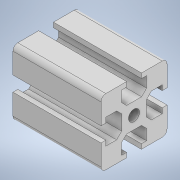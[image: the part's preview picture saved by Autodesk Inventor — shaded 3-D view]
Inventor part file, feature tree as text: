
AUTODESK INVENTOR PART (.ipt)
format: ipt  version: 2020.2 (Build 242310000, 310)  size: 175,104 bytes
history: native  units: in
note: dims shown in document units (in); Inventor stores cm internally (conversion verified against a paired STEP export)
features: extrude x1, sketch x1
ambient origin geometry x8: Origin, YZ Plane, XZ Plane, XY Plane, X Axis, Y Axis, Z Axis, Center Point
bodies: Solid1 (feature_tree)
feature tree (2):
  extrude  "Extrusion1"  Depth=0.29in
  sketch  "Sketch2"  dims[d9=0.2325in d18=0.055in d20=0.055in d34=0.29in d35=0.055in d37=0.058in d38=0.1225in d39=0.081in d40=135.0deg d41=0.17in d42=0.081in d43=0.058in d44=0.055in d45=0.75in d46=0.055in d47=1.5748in d49=360.0deg d51=0.2348in d52=0.232in d56=0.75in d58=0.125in d61=0.055in d62=0.055in d63=0.055in d64=0.055in d65=1.5748in d67=360.0deg d69=1.0in d70=0.0in d71=0.1225in]
